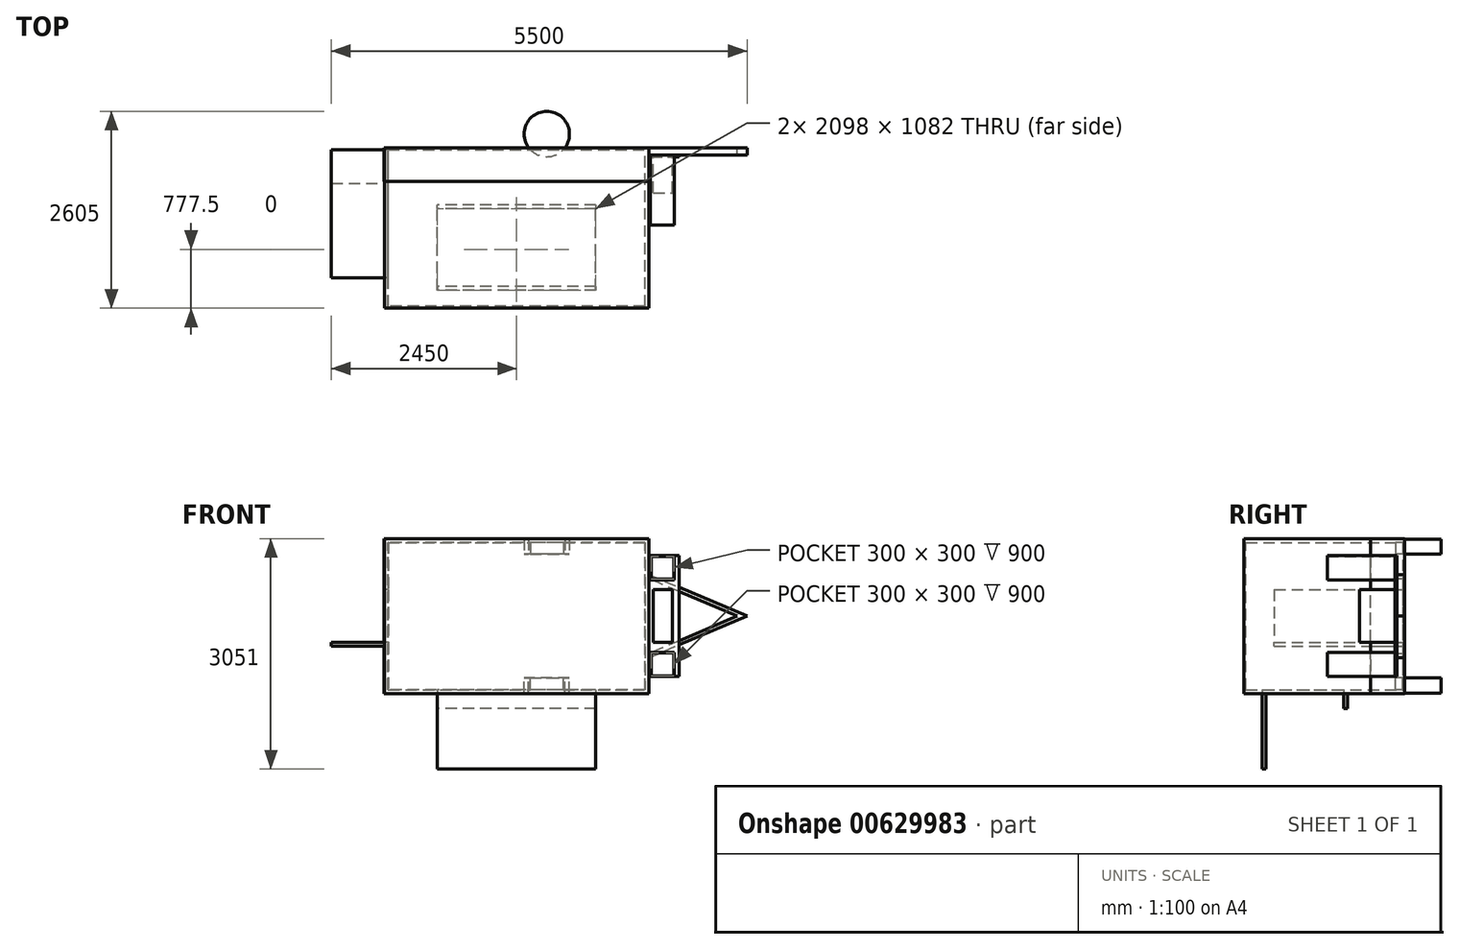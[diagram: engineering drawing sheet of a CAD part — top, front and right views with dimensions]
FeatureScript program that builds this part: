
annotation { "Feature Type Name" : "Feature", "Feature Type Description" : "" }
export const myFeature = defineFeature(function(context is Context, id is Id, definition is map)
    precondition{}
    {
        {
            var Q0;
            Q0=qCreatedBy(makeId("Front.planeOp"),FACE);
            var sketch = newSketch(context, id + "F0", { "sketchPlane" : qUnion([Q0])});
            skLineSegment(sketch, "E0.bottom", {"start": v(1750, -1025) * mm, "end": v(-1750, -1025) * mm});
            skLineSegment(sketch, "E0.top", {"start": v(1750, 1025) * mm, "end": v(-1750, 1025) * mm});
            skLineSegment(sketch, "E0.left", {"start": v(1750, -1025) * mm, "end": v(1750, 1025) * mm});
            skLineSegment(sketch, "E0.right", {"start": v(-1750, -1025) * mm, "end": v(-1750, 1025) * mm});
            skPoint(sketch, "E0.middle", {"position": v(0, 0) * mm});
            skLineSegment(sketch, "E1.0", {"start": v(1700, 975) * mm, "end": v(-1700, 975) * mm});
            skLineSegment(sketch, "E1.1", {"start": v(1700, -975) * mm, "end": v(1700, 975) * mm});
            skLineSegment(sketch, "E1.2", {"start": v(1700, -975) * mm, "end": v(-1700, -975) * mm});
            skLineSegment(sketch, "E1.3", {"start": v(-1700, -975) * mm, "end": v(-1700, 975) * mm});
            skSolve(sketch);
        }
        {
            var Q0;
            Q0=makeQuery(id+"F0.imprint","IMPRINT",FACE,{"disambiguationData":[TD([[makeQuery(id+"F0.imprint","IMPRINT",EDGE,{"derivedFrom":sQuery(id+"F0.wireOp",EDGE,"E0.bottom")}),-1.0]])]});
            var Q1;
            Q1=sQuery(id+"F0.wireOp",EDGE,"E0.top");
            var Q2;
            Q2=sQuery(id+"F0.wireOp",EDGE,"E0.right");
            var Q3;
            Q3=sQuery(id+"F0.wireOp",EDGE,"E0.bottom");
            var Q4;
            Q4=sQuery(id+"F0.wireOp",EDGE,"E0.left");
            extrude(context, id + "F1", {"entities" : qUnion([Q0]), "surfaceEntities" : qUnion([Q1, Q2, Q3, Q4]), "depth" : 2100 * mm, "offsetDistance" : 25 * mm});
        }
        {
            var Q0;
            Q0=makeQuery(id+"F1.opExtrude","SWEPT_FACE",FACE,{"disambiguationData":[OSD([sQuery(id+"F0.wireOp",EDGE,"E0.bottom")])]});
            var sketch = newSketch(context, id + "F2", { "sketchPlane" : qUnion([Q0])});
            skSolve(sketch);
        }
        {
            var Q0;
            Q0=qCreatedBy(makeId("Top.planeOp"),FACE);
            cPlane(context, id + "F3", {"entities" : qUnion([Q0]), "cplaneType" : CPlaneType.OFFSET, "offset" : 2040 * mm / 2 - 200 * mm, "width" : 150 * mm, "height" : 150 * mm});
        }
        {
            var Q0;
            Q0=qCreatedBy(id+"F3.planeOp",FACE);
            var sketch = newSketch(context, id + "F4", { "sketchPlane" : qUnion([Q0])});
            skCircle(sketch, "E2", {"center": v(400, 180) * mm, "radius": 300 * mm});
            skCircle(sketch, "E3.MirrorC", {"center": v(-400, 180) * mm, "radius": 300 * mm});
            skSolve(sketch);
        }
        {
            var Q0;
            Q0=makeQuery(id+"F4.imprint","IMPRINT",FACE,{"disambiguationData":[TD([[makeQuery(id+"F4.imprint","IMPRINT",EDGE,{"derivedFrom":sQuery(id+"F4.wireOp",EDGE,"E2")}),1.0]])]});
            var Q1;
            Q1=makeQuery(id+"F4.imprint","IMPRINT",FACE,{"disambiguationData":[TD([[makeQuery(id+"F4.imprint","IMPRINT",EDGE,{"derivedFrom":sQuery(id+"F4.wireOp",EDGE,"E3.MirrorC")}),-1.0]])]});
            extrude(context, id + "F5", {"entities" : qUnion([Q0, Q1]), "depth" : 200 * mm, "offsetDistance" : 25 * mm});
        }
        {
            var Q0;
            Q0=makeQuery(id+"F5.opExtrude","SWEPT_BODY",BODY,{"disambiguationData":[OSD([sQuery(id+"F4.wireOp",EDGE,"E3.MirrorC")])]});
            var Q1;
            Q1=makeQuery(id+"F5.opExtrude","SWEPT_BODY",BODY,{"disambiguationData":[OSD([sQuery(id+"F4.wireOp",EDGE,"E2")])]});
            var Q2;
            Q2=qCreatedBy(makeId("Top.planeOp"),FACE);
            mirror(context, id + "F6", {"entities" : qUnion([Q0, Q1]), "mirrorPlane" : qUnion([Q2])});
        }
        {
            var Q0;
            Q0=makeQuery(id+"F1.opExtrude","CAP_FACE",FACE,{"disambiguationData":[OSD([sQuery(id+"F0.wireOp",EDGE,"E0.bottom"),sQuery(id+"F0.wireOp",EDGE,"E0.top"),sQuery(id+"F0.wireOp",EDGE,"E0.left"),sQuery(id+"F0.wireOp",EDGE,"E0.right")])],"isStart":true});
            var sketch = newSketch(context, id + "F7", { "sketchPlane" : qUnion([Q0])});
            skLineSegment(sketch, "E4", {"start": v(0, 0) * mm, "end": v(-3050, 0) * mm, "construction": true});
            skLineSegment(sketch, "E5", {"start": v(-1750, 0) * mm, "end": v(-1750, 550) * mm, "construction": true});
            skLineSegment(sketch, "E6", {"start": v(-1750, 550) * mm, "end": v(-3050, 0) * mm});
            skLineSegment(sketch, "E7", {"start": v(-2921.68, 0) * mm, "end": v(-1750, 495.7) * mm});
            skLineSegment(sketch, "E8", {"start": v(-1750, 495.7) * mm, "end": v(-1750, 550) * mm});
            skLineSegment(sketch, "E9.MirrorCS", {"start": v(-2921.68, 0) * mm, "end": v(-1750, -495.7) * mm});
            skLineSegment(sketch, "E10.MirrorCS", {"start": v(-1750, -550) * mm, "end": v(-3050, 0) * mm});
            skLineSegment(sketch, "E11.MirrorCS", {"start": v(-1750, -495.7) * mm, "end": v(-1750, -550) * mm});
            skSolve(sketch);
        }
        {
            var Q0;
            Q0=makeQuery(id+"F7.imprint","IMPRINT",FACE,{"disambiguationData":[TD([[makeQuery(id+"F7.imprint","IMPRINT",EDGE,{"derivedFrom":sQuery(id+"F7.wireOp",EDGE,"E6")}),1.0]])]});
            extrude(context, id + "F8", {"entities" : qUnion([Q0]), "oppositeDirection" : true, "depth" : 100 * mm, "offsetDistance" : 25 * mm});
        }
        {
            var Q0;
            Q0=makeQuery(id+"F8.opExtrude","CAP_FACE",FACE,{"disambiguationData":[OSD([sQuery(id+"F7.wireOp",EDGE,"E6"),sQuery(id+"F7.wireOp",EDGE,"E7"),sQuery(id+"F7.wireOp",EDGE,"E8"),sQuery(id+"F7.wireOp",EDGE,"E9.MirrorCS"),sQuery(id+"F7.wireOp",EDGE,"E10.MirrorCS"),sQuery(id+"F7.wireOp",EDGE,"E11.MirrorCS")])],"isStart":false});
            var sketch = newSketch(context, id + "F9", { "sketchPlane" : qUnion([Q0])});
            skLineSegment(sketch, "E12.bottom", {"start": v(1810, -350) * mm, "end": v(2060, -350) * mm});
            skLineSegment(sketch, "E12.top", {"start": v(1810, 350) * mm, "end": v(2060, 350) * mm});
            skLineSegment(sketch, "E12.left", {"start": v(1810, -350) * mm, "end": v(1810, 350) * mm});
            skLineSegment(sketch, "E12.right", {"start": v(2060, -350) * mm, "end": v(2060, 350) * mm});
            skSolve(sketch);
        }
        {
            var Q0;
            {var subQ0=sQuery(id+"F9.wireOp",EDGE,"E12.right");var subQ1=sQuery(id+"F9.wireOp",EDGE,"E12.top");var subQ2=makeQuery(id+"F9.imprint","INTERSECT",VERTEX,{"derivedFrom":[subQ1,subQ0]});Q0=makeQuery(id+"F9.imprint","IMPRINT",FACE,{"disambiguationData":[TD([[makeQuery(id+"F9.imprint","IMPRINT",EDGE,{"disambiguationData":[TD([[subQ2,1.0]])],"derivedFrom":subQ1}),-1.0]])]});}
            var Q1;
            {var subQ0=sQuery(id+"F9.wireOp",EDGE,"E12.top");var subQ1=makeQuery(id+"F8.opExtrude","CAP_EDGE",EDGE,{"disambiguationData":[OSD([sQuery(id+"F7.wireOp",EDGE,"E7")])],"isStart":false});var subQ2=makeQuery(id+"F9.imprint","INTERSECT",VERTEX,{"derivedFrom":[subQ1,subQ0]});Q1=makeQuery(id+"F9.imprint","IMPRINT",FACE,{"disambiguationData":[TD([[makeQuery(id+"F9.imprint","IMPRINT",EDGE,{"disambiguationData":[TD([[subQ2,-1.0]])],"derivedFrom":subQ0}),-1.0]])]});}
            var Q2;
            {var subQ0=sQuery(id+"F9.wireOp",EDGE,"E12.top");var subQ7=sQuery(id+"F9.wireOp",EDGE,"E12.left");var subQ8=makeQuery(id+"F9.imprint","INTERSECT",VERTEX,{"derivedFrom":[subQ0,subQ7]});Q2=makeQuery(id+"F9.imprint","IMPRINT",FACE,{"disambiguationData":[TD([[makeQuery(id+"F9.imprint","IMPRINT",EDGE,{"disambiguationData":[TD([[subQ8,-1.0]])],"derivedFrom":subQ0}),-1.0]])]});}
            var Q3;
            {var subQ0=sQuery(id+"F9.wireOp",EDGE,"E12.left");var subQ1=makeQuery(id+"F8.opExtrude","CAP_EDGE",EDGE,{"disambiguationData":[OSD([sQuery(id+"F7.wireOp",EDGE,"E10.MirrorCS")])],"isStart":false});var subQ2=makeQuery(id+"F9.imprint","INTERSECT",VERTEX,{"derivedFrom":[subQ1,subQ0]});Q3=makeQuery(id+"F9.imprint","IMPRINT",FACE,{"disambiguationData":[TD([[makeQuery(id+"F9.imprint","IMPRINT",EDGE,{"disambiguationData":[TD([[subQ2,-1.0]])],"derivedFrom":subQ0}),-1.0]])]});}
            var Q4;
            {var subQ0=sQuery(id+"F9.wireOp",EDGE,"E12.bottom");Q4=makeQuery(id+"F9.imprint","IMPRINT",FACE,{"disambiguationData":[TD([[makeQuery(id+"F9.imprint","IMPRINT",EDGE,{"derivedFrom":subQ0}),1.0]])]});}
            extrude(context, id + "F10", {"entities" : qUnion([Q0, Q1, Q2, Q3, Q4]), "depth" : 500 * mm, "offsetDistance" : 25 * mm});
        }
        {
            var Q0;
            Q0=makeQuery(id+"F1.opExtrude","CAP_FACE",FACE,{"disambiguationData":[OSD([sQuery(id+"F0.wireOp",EDGE,"E0.bottom"),sQuery(id+"F0.wireOp",EDGE,"E0.top"),sQuery(id+"F0.wireOp",EDGE,"E0.left"),sQuery(id+"F0.wireOp",EDGE,"E0.right"),sQuery(id+"F0.wireOp",EDGE,"E1.0"),sQuery(id+"F0.wireOp",EDGE,"E1.1"),sQuery(id+"F0.wireOp",EDGE,"E1.2"),sQuery(id+"F0.wireOp",EDGE,"E1.3")])],"isStart":true});
            var sketch = newSketch(context, id + "F11", { "sketchPlane" : qUnion([Q0])});
            skLineSegment(sketch, "E13.bottom", {"start": v(1750, -1025) * mm, "end": v(-1750, -1025) * mm});
            skLineSegment(sketch, "E13.top", {"start": v(1750, 1025) * mm, "end": v(-1750, 1025) * mm});
            skLineSegment(sketch, "E13.left", {"start": v(1750, -1025) * mm, "end": v(1750, 1025) * mm});
            skLineSegment(sketch, "E13.right", {"start": v(-1750, -1025) * mm, "end": v(-1750, 1025) * mm});
            skSolve(sketch);
        }
        {
            var Q0;
            Q0 = qSketchRegion(id + "F11", true);
            extrude(context, id + "F12", {"entities" : qUnion([Q0]), "operationType" : NewBodyOperationType.ADD, "oppositeDirection" : true, "depth" : 25 * mm, "offsetDistance" : 25 * mm});
        }
        {
            var Q0;
            Q0=makeQuery(id+"F1.opExtrude","CAP_FACE",FACE,{"disambiguationData":[OSD([sQuery(id+"F0.wireOp",EDGE,"E0.bottom"),sQuery(id+"F0.wireOp",EDGE,"E0.top"),sQuery(id+"F0.wireOp",EDGE,"E0.left"),sQuery(id+"F0.wireOp",EDGE,"E0.right"),sQuery(id+"F0.wireOp",EDGE,"E1.0"),sQuery(id+"F0.wireOp",EDGE,"E1.1"),sQuery(id+"F0.wireOp",EDGE,"E1.2"),sQuery(id+"F0.wireOp",EDGE,"E1.3")])],"isStart":false});
            var sketch = newSketch(context, id + "F13", { "sketchPlane" : qUnion([Q0])});
            skLineSegment(sketch, "E14.bottom", {"start": v(-1750, 1025) * mm, "end": v(1750, 1025) * mm});
            skLineSegment(sketch, "E14.top", {"start": v(-1750, -1025) * mm, "end": v(1750, -1025) * mm});
            skLineSegment(sketch, "E14.left", {"start": v(-1750, 1025) * mm, "end": v(-1750, -1025) * mm});
            skLineSegment(sketch, "E14.right", {"start": v(1750, 1025) * mm, "end": v(1750, -1025) * mm});
            skSolve(sketch);
        }
        {
            var Q0;
            Q0 = qSketchRegion(id + "F13", true);
            extrude(context, id + "F14", {"entities" : qUnion([Q0]), "operationType" : NewBodyOperationType.ADD, "depth" : 25 * mm, "offsetDistance" : 25 * mm});
        }
        {
            var Q0;
            {var subQ0=sQuery(id+"F0.wireOp",EDGE,"E0.bottom");Q0=makeQuery(id+"F2.imprint","IMPRINT",FACE,{"disambiguationData":[TD([[makeQuery(id+"F2.imprint","IMPRINT",EDGE,{"derivedFrom":makeQuery(id+"F1.opExtrude","CAP_EDGE",EDGE,{"disambiguationData":[OSD([subQ0])],"isStart":true})}),-1.0]])]});}
            var sketch = newSketch(context, id + "F15", { "sketchPlane" : qUnion([Q0])});
            skLineSegment(sketch, "E15.bottom", {"start": v(1049, 1888.5) * mm, "end": v(-1049, 1888.5) * mm});
            skLineSegment(sketch, "E15.top", {"start": v(1049, 806.5) * mm, "end": v(-1049, 806.5) * mm});
            skLineSegment(sketch, "E15.left", {"start": v(1049, 1888.5) * mm, "end": v(1049, 806.5) * mm});
            skLineSegment(sketch, "E15.right", {"start": v(-1049, 1888.5) * mm, "end": v(-1049, 806.5) * mm});
            skSolve(sketch);
        }
        {
            var Q0;
            Q0=makeQuery(id+"F15.imprint","IMPRINT",FACE,{"disambiguationData":[TD([[makeQuery(id+"F15.imprint","IMPRINT",EDGE,{"derivedFrom":sQuery(id+"F15.wireOp",EDGE,"E15.bottom")}),1.0]])]});
            extrude(context, id + "F16", {"entities" : qUnion([Q0]), "operationType" : NewBodyOperationType.REMOVE, "oppositeDirection" : true, "depth" : 260 * mm, "offsetDistance" : 25 * mm});
        }
        {
            var Q0;
            Q0=makeQuery(id+"F14.boolean.opBoolean","MERGE",FACE,{"derivedFrom":[makeQuery(id+"F1.opExtrude","SWEPT_FACE",FACE,{"disambiguationData":[OSD([sQuery(id+"F0.wireOp",EDGE,"E0.right")])]}),makeQuery(id+"F14.opExtrude","SWEPT_FACE",FACE,{"disambiguationData":[OSD([sQuery(id+"F13.wireOp",EDGE,"E14.left")])]})]});
            var sketch = newSketch(context, id + "F17", { "sketchPlane" : qUnion([Q0])});
            skLineSegment(sketch, "E16.bottom", {"start": v(1725, 350) * mm, "end": v(25, 350) * mm});
            skLineSegment(sketch, "E16.top", {"start": v(1725, -350) * mm, "end": v(25, -350) * mm});
            skLineSegment(sketch, "E16.left", {"start": v(1725, 350) * mm, "end": v(1725, -350) * mm});
            skLineSegment(sketch, "E16.right", {"start": v(25, 350) * mm, "end": v(25, -350) * mm});
            skSolve(sketch);
        }
        {
            var Q0;
            Q0=makeQuery(id+"F17.imprint","IMPRINT",FACE,{"disambiguationData":[TD([[makeQuery(id+"F17.imprint","IMPRINT",EDGE,{"derivedFrom":sQuery(id+"F17.wireOp",EDGE,"E16.bottom")}),1.0]])]});
            extrude(context, id + "F18", {"entities" : qUnion([Q0]), "operationType" : NewBodyOperationType.REMOVE, "oppositeDirection" : true, "depth" : 150 * mm, "offsetDistance" : 25 * mm});
        }
        {
            var Q0;
            Q0=makeQuery(id+"F16.boolean.opBoolean","COPY",FACE,{"derivedFrom":makeQuery(id+"F16.opExtrude","SWEPT_FACE",FACE,{"disambiguationData":[OSD([sQuery(id+"F15.wireOp",EDGE,"E15.right")])]})});
            var sketch = newSketch(context, id + "F19", { "sketchPlane" : qUnion([Q0])});
            skLineSegment(sketch, "E17.bottom", {"start": v(-806.5, -1025) * mm, "end": v(-756.5, -1025) * mm});
            skLineSegment(sketch, "E17.top", {"start": v(-806.5, -1225) * mm, "end": v(-756.5, -1225) * mm});
            skLineSegment(sketch, "E17.left", {"start": v(-806.5, -1025) * mm, "end": v(-806.5, -1225) * mm});
            skLineSegment(sketch, "E17.right", {"start": v(-756.5, -1025) * mm, "end": v(-756.5, -1225) * mm});
            skSolve(sketch);
        }
        {
            var Q0;
            Q0=makeQuery(id+"F19.imprint","IMPRINT",FACE,{"disambiguationData":[TD([[makeQuery(id+"F19.imprint","IMPRINT",EDGE,{"derivedFrom":sQuery(id+"F19.wireOp",EDGE,"E17.bottom")}),-1.0]])]});
            var Q1;
            Q1=makeQuery(id+"F16.boolean.opBoolean","COPY",FACE,{"derivedFrom":makeQuery(id+"F16.opExtrude","SWEPT_FACE",FACE,{"disambiguationData":[OSD([sQuery(id+"F15.wireOp",EDGE,"E15.left")])]})});
            extrude(context, id + "F20", {"entities" : qUnion([Q0]), "endBound" : BoundingType.UP_TO_SURFACE, "depth" : 25 * mm, "endBoundEntityFace" : qUnion([Q1]), "offsetDistance" : 25 * mm});
        }
        {
            var Q0;
            Q0=makeQuery(id+"F16.boolean.opBoolean","COPY",FACE,{"derivedFrom":makeQuery(id+"F16.opExtrude","SWEPT_FACE",FACE,{"disambiguationData":[OSD([sQuery(id+"F15.wireOp",EDGE,"E15.right")])]})});
            var sketch = newSketch(context, id + "F21", { "sketchPlane" : qUnion([Q0])});
            skLineSegment(sketch, "E18.bottom", {"start": v(-1888.5, -1025) * mm, "end": v(-1888.5, -1025) * mm});
            skLineSegment(sketch, "E18.top", {"start": v(-1838.5, -2025) * mm, "end": v(-1888.5, -2025) * mm});
            skLineSegment(sketch, "E18.left", {"start": v(-1838.5, -1025) * mm, "end": v(-1838.5, -2025) * mm});
            skLineSegment(sketch, "E18.right", {"start": v(-1888.5, -1025) * mm, "end": v(-1888.5, -2025) * mm});
            skSolve(sketch);
        }
        {
            var Q0;
            Q0=makeQuery(id+"F21.imprint","IMPRINT",FACE,{"disambiguationData":[TD([[makeQuery(id+"F21.imprint","IMPRINT",EDGE,{"derivedFrom":sQuery(id+"F21.wireOp",EDGE,"E18.bottom")}),1.0]])]});
            var Q1;
            Q1=makeQuery(id+"F21.imprint","IMPRINT",FACE,{"disambiguationData":[TD([[makeQuery(id+"F21.imprint","IMPRINT",EDGE,{"derivedFrom":sQuery(id+"F21.wireOp",EDGE,"E18.top")}),-1.0]])]});
            var Q2;
            Q2=makeQuery(id+"F16.boolean.opBoolean","COPY",FACE,{"derivedFrom":makeQuery(id+"F16.opExtrude","SWEPT_FACE",FACE,{"disambiguationData":[OSD([sQuery(id+"F15.wireOp",EDGE,"E15.left")])]})});
            extrude(context, id + "F22", {"entities" : qUnion([Q0, Q1]), "endBound" : BoundingType.UP_TO_SURFACE, "depth" : 25 * mm, "endBoundEntityFace" : qUnion([Q2]), "offsetDistance" : 25 * mm});
        }
        {
            var Q0;
            Q0=makeQuery(id+"F18.boolean.opBoolean","MERGE",FACE,{"derivedFrom":[makeQuery(id+"F12.opExtrude","CAP_FACE",FACE,{"disambiguationData":[OSD([sQuery(id+"F11.wireOp",EDGE,"E13.bottom"),sQuery(id+"F11.wireOp",EDGE,"E13.top"),sQuery(id+"F11.wireOp",EDGE,"E13.left"),sQuery(id+"F11.wireOp",EDGE,"E13.right")])],"isStart":false}),makeQuery(id+"F18.opExtrude","SWEPT_FACE",FACE,{"disambiguationData":[OSD([sQuery(id+"F17.wireOp",EDGE,"E16.right")])]})]});
            var sketch = newSketch(context, id + "F23", { "sketchPlane" : qUnion([Q0])});
            skLineSegment(sketch, "E19.bottom", {"start": v(-1750, -350) * mm, "end": v(-2450, -350) * mm});
            skLineSegment(sketch, "E19.top", {"start": v(-1750, -400) * mm, "end": v(-2450, -400) * mm});
            skLineSegment(sketch, "E19.left", {"start": v(-1750, -350) * mm, "end": v(-1750, -400) * mm});
            skLineSegment(sketch, "E19.right", {"start": v(-2450, -350) * mm, "end": v(-2450, -400) * mm});
            skSolve(sketch);
        }
        {
            var Q0;
            Q0=makeQuery(id+"F23.imprint","IMPRINT",FACE,{"disambiguationData":[TD([[makeQuery(id+"F23.imprint","IMPRINT",EDGE,{"derivedFrom":sQuery(id+"F23.wireOp",EDGE,"E19.bottom")}),1.0]])]});
            var Q1;
            Q1=makeQuery(id+"F18.boolean.opBoolean","COPY",FACE,{"derivedFrom":makeQuery(id+"F18.opExtrude","SWEPT_FACE",FACE,{"disambiguationData":[OSD([sQuery(id+"F17.wireOp",EDGE,"E16.left")])]})});
            extrude(context, id + "F24", {"entities" : qUnion([Q0]), "endBound" : BoundingType.UP_TO_SURFACE, "depth" : 25 * mm, "endBoundEntityFace" : qUnion([Q1]), "offsetDistance" : 25 * mm});
        }
        {
            var Q0;
            Q0=makeQuery(id+"F8.opExtrude","CAP_FACE",FACE,{"disambiguationData":[OSD([sQuery(id+"F7.wireOp",EDGE,"E6"),sQuery(id+"F7.wireOp",EDGE,"E7"),sQuery(id+"F7.wireOp",EDGE,"E8"),sQuery(id+"F7.wireOp",EDGE,"E9.MirrorCS"),sQuery(id+"F7.wireOp",EDGE,"E10.MirrorCS"),sQuery(id+"F7.wireOp",EDGE,"E11.MirrorCS")])],"isStart":false});
            var sketch = newSketch(context, id + "F25", { "sketchPlane" : qUnion([Q0])});
            skLineSegment(sketch, "E20.bottom", {"start": v(1750, 800) * mm, "end": v(2150, 800) * mm});
            skLineSegment(sketch, "E20.top", {"start": v(1750, -800) * mm, "end": v(2150, -800) * mm});
            skLineSegment(sketch, "E20.left", {"start": v(1750, 800) * mm, "end": v(1750, -800) * mm});
            skLineSegment(sketch, "E20.right", {"start": v(2150, 800) * mm, "end": v(2150, -800) * mm});
            skSolve(sketch);
        }
        {
            var Q0;
            {var subQ0=sQuery(id+"F25.wireOp",EDGE,"E20.top");Q0=makeQuery(id+"F25.imprint","IMPRINT",FACE,{"disambiguationData":[TD([[makeQuery(id+"F25.imprint","IMPRINT",EDGE,{"derivedFrom":subQ0}),1.0]])]});}
            var Q1;
            {var subQ0=sQuery(id+"F25.wireOp",EDGE,"E20.left");var subQ1=makeQuery(id+"F8.opExtrude","CAP_EDGE",EDGE,{"disambiguationData":[OSD([sQuery(id+"F7.wireOp",EDGE,"E7")])],"isStart":false});var subQ2=makeQuery(id+"F25.imprint","INTERSECT",VERTEX,{"derivedFrom":[subQ1,subQ0]});Q1=makeQuery(id+"F25.imprint","IMPRINT",FACE,{"disambiguationData":[TD([[makeQuery(id+"F25.imprint","IMPRINT",EDGE,{"disambiguationData":[TD([[subQ2,-1.0]])],"derivedFrom":subQ0}),1.0]])]});}
            var Q2;
            {var subQ0=sQuery(id+"F25.wireOp",EDGE,"E20.left");var subQ1=makeQuery(id+"F8.opExtrude","CAP_EDGE",EDGE,{"disambiguationData":[OSD([sQuery(id+"F7.wireOp",EDGE,"E6")])],"isStart":false});var subQ2=makeQuery(id+"F25.imprint","INTERSECT",VERTEX,{"derivedFrom":[subQ1,subQ0]});Q2=makeQuery(id+"F25.imprint","IMPRINT",FACE,{"disambiguationData":[TD([[makeQuery(id+"F25.imprint","IMPRINT",EDGE,{"disambiguationData":[TD([[subQ2,-1.0]])],"derivedFrom":subQ0}),1.0]])]});}
            var Q3;
            {var subQ0=sQuery(id+"F25.wireOp",EDGE,"E20.bottom");Q3=makeQuery(id+"F25.imprint","IMPRINT",FACE,{"disambiguationData":[TD([[makeQuery(id+"F25.imprint","IMPRINT",EDGE,{"derivedFrom":subQ0}),-1.0]])]});}
            var Q4;
            {var subQ0=sQuery(id+"F25.wireOp",EDGE,"E20.left");var subQ1=makeQuery(id+"F8.opExtrude","CAP_EDGE",EDGE,{"disambiguationData":[OSD([sQuery(id+"F7.wireOp",EDGE,"E9.MirrorCS")])],"isStart":false});var subQ2=makeQuery(id+"F25.imprint","INTERSECT",VERTEX,{"derivedFrom":[subQ1,subQ0]});Q4=makeQuery(id+"F25.imprint","IMPRINT",FACE,{"disambiguationData":[TD([[makeQuery(id+"F25.imprint","IMPRINT",EDGE,{"disambiguationData":[TD([[subQ2,-1.0]])],"derivedFrom":subQ0}),1.0]])]});}
            var Q5;
            {var subQ0=sQuery(id+"F25.wireOp",EDGE,"E20.left");var subQ1=makeQuery(id+"F8.opExtrude","CAP_EDGE",EDGE,{"disambiguationData":[OSD([sQuery(id+"F7.wireOp",EDGE,"E6")])],"isStart":false});var subQ2=makeQuery(id+"F25.imprint","INTERSECT",VERTEX,{"derivedFrom":[subQ1,subQ0]});var subQ3=makeQuery(id+"F8.opExtrude","CAP_EDGE",EDGE,{"disambiguationData":[OSD([sQuery(id+"F7.wireOp",EDGE,"E7")])],"isStart":false});var subQ4=makeQuery(id+"F25.imprint","INTERSECT",VERTEX,{"derivedFrom":[subQ3,subQ0]});Q5=makeQuery(id+"F25.imprint","IMPRINT",FACE,{"disambiguationData":[TD([[makeQuery(id+"F25.imprint","IMPRINT",EDGE,{"disambiguationData":[TD([[subQ2,1.0],[subQ4,-1.0]])],"derivedFrom":subQ0}),-1.0]])]});}
            var Q6;
            {var subQ0=sQuery(id+"F25.wireOp",EDGE,"E20.left");var subQ1=makeQuery(id+"F8.opExtrude","CAP_EDGE",EDGE,{"disambiguationData":[OSD([sQuery(id+"F7.wireOp",EDGE,"E9.MirrorCS")])],"isStart":false});var subQ2=makeQuery(id+"F25.imprint","INTERSECT",VERTEX,{"derivedFrom":[subQ1,subQ0]});var subQ3=makeQuery(id+"F8.opExtrude","CAP_EDGE",EDGE,{"disambiguationData":[OSD([sQuery(id+"F7.wireOp",EDGE,"E10.MirrorCS")])],"isStart":false});var subQ4=makeQuery(id+"F25.imprint","INTERSECT",VERTEX,{"derivedFrom":[subQ3,subQ0]});Q6=makeQuery(id+"F25.imprint","IMPRINT",FACE,{"disambiguationData":[TD([[makeQuery(id+"F25.imprint","IMPRINT",EDGE,{"disambiguationData":[TD([[subQ2,1.0],[subQ4,-1.0]])],"derivedFrom":subQ0}),-1.0]])]});}
            extrude(context, id + "F26", {"entities" : qUnion([Q0, Q1, Q2, Q3, Q4, Q5, Q6]), "depth" : 25 * mm, "offsetDistance" : 25 * mm});
        }
        {
            var Q0;
            Q0=makeQuery(id+"F26.opExtrude","CAP_FACE",FACE,{"disambiguationData":[OSD([sQuery(id+"F25.wireOp",EDGE,"E20.bottom"),sQuery(id+"F25.wireOp",EDGE,"E20.top"),sQuery(id+"F25.wireOp",EDGE,"E20.left"),sQuery(id+"F25.wireOp",EDGE,"E20.right")])],"isStart":false});
            var sketch = newSketch(context, id + "F27", { "sketchPlane" : qUnion([Q0])});
            skLineSegment(sketch, "E21.bottom", {"start": v(1770, 800) * mm, "end": v(2090, 800) * mm});
            skLineSegment(sketch, "E21.top", {"start": v(1770, 480) * mm, "end": v(2090, 480) * mm});
            skLineSegment(sketch, "E21.left", {"start": v(1770, 800) * mm, "end": v(1770, 480) * mm});
            skLineSegment(sketch, "E21.right", {"start": v(2090, 800) * mm, "end": v(2090, 480) * mm});
            skLineSegment(sketch, "E22.0", {"start": v(1780, 790) * mm, "end": v(2080, 790) * mm});
            skLineSegment(sketch, "E22.1", {"start": v(1780, 790) * mm, "end": v(1780, 490) * mm});
            skLineSegment(sketch, "E22.2", {"start": v(1780, 490) * mm, "end": v(2080, 490) * mm});
            skLineSegment(sketch, "E22.3", {"start": v(2080, 790) * mm, "end": v(2080, 490) * mm});
            skLineSegment(sketch, "E23.MirrorCS", {"start": v(1770, -800) * mm, "end": v(2090, -800) * mm});
            skLineSegment(sketch, "E24.MirrorCS", {"start": v(1780, -790) * mm, "end": v(2080, -790) * mm});
            skLineSegment(sketch, "E25.MirrorCS", {"start": v(1770, -800) * mm, "end": v(1770, -480) * mm});
            skLineSegment(sketch, "E26.MirrorCS", {"start": v(1780, -790) * mm, "end": v(1780, -490) * mm});
            skLineSegment(sketch, "E27.MirrorCS", {"start": v(1780, -490) * mm, "end": v(2080, -490) * mm});
            skLineSegment(sketch, "E28.MirrorCS", {"start": v(1770, -480) * mm, "end": v(2090, -480) * mm});
            skLineSegment(sketch, "E29.MirrorCS", {"start": v(2080, -790) * mm, "end": v(2080, -490) * mm});
            skLineSegment(sketch, "E30.MirrorCS", {"start": v(2090, -800) * mm, "end": v(2090, -480) * mm});
            skSolve(sketch);
        }
        {
            var Q0;
            Q0=makeQuery(id+"F27.imprint","IMPRINT",FACE,{"disambiguationData":[TD([[makeQuery(id+"F27.imprint","IMPRINT",EDGE,{"derivedFrom":sQuery(id+"F27.wireOp",EDGE,"E21.bottom")}),-1.0]])]});
            var Q1;
            Q1=makeQuery(id+"F27.imprint","IMPRINT",FACE,{"disambiguationData":[TD([[makeQuery(id+"F27.imprint","IMPRINT",EDGE,{"derivedFrom":sQuery(id+"F27.wireOp",EDGE,"E23.MirrorCS")}),1.0]])]});
            extrude(context, id + "F28", {"entities" : qUnion([Q0, Q1]), "operationType" : NewBodyOperationType.ADD, "depth" : 900 * mm, "offsetDistance" : 25 * mm});
        }
        {
            var Q0;
            Q0=makeQuery(id+"F24.opExtrude","SWEPT_FACE",FACE,{"disambiguationData":[OSD([sQuery(id+"F23.wireOp",EDGE,"E19.top")])]});
            var sketch = newSketch(context, id + "F29", { "sketchPlane" : qUnion([Q0])});
            skLineSegment(sketch, "E31.bottom", {"start": v(-2450, 25) * mm, "end": v(-1750, 25) * mm});
            skLineSegment(sketch, "E31.top", {"start": v(-2450, 475) * mm, "end": v(-1750, 475) * mm});
            skLineSegment(sketch, "E31.left", {"start": v(-2450, 25) * mm, "end": v(-2450, 475) * mm});
            skLineSegment(sketch, "E31.right", {"start": v(-1750, 25) * mm, "end": v(-1750, 475) * mm});
            skSolve(sketch);
        }
        {
            var Q0;
            Q0=makeQuery(id+"F29.imprint","IMPRINT",FACE,{"disambiguationData":[TD([[makeQuery(id+"F29.imprint","IMPRINT",EDGE,{"derivedFrom":sQuery(id+"F29.wireOp",EDGE,"E31.bottom")}),-1.0]])]});
            extrude(context, id + "F30", {"entities" : qUnion([Q0]), "depth" : 1 * mm, "offsetDistance" : 25 * mm});
        }
        {
            var Q0;
            Q0=makeQuery(id+"F14.boolean.opBoolean","MERGE",FACE,{"derivedFrom":[makeQuery(id+"F1.opExtrude","SWEPT_FACE",FACE,{"disambiguationData":[OSD([sQuery(id+"F0.wireOp",EDGE,"E0.right")])]}),makeQuery(id+"F14.opExtrude","SWEPT_FACE",FACE,{"disambiguationData":[OSD([sQuery(id+"F13.wireOp",EDGE,"E14.left")])]})]});
            var sketch = newSketch(context, id + "F31", { "sketchPlane" : qUnion([Q0])});
            skLineSegment(sketch, "E32.bottom", {"start": v(0, 1025) * mm, "end": v(450, 1025) * mm});
            skLineSegment(sketch, "E32.top", {"start": v(0, -1025) * mm, "end": v(450, -1025) * mm});
            skLineSegment(sketch, "E32.left", {"start": v(0, 1025) * mm, "end": v(0, -1025) * mm});
            skLineSegment(sketch, "E32.right", {"start": v(450, 1025) * mm, "end": v(450, -1025) * mm});
            skSolve(sketch);
        }
        {
            var Q0;
            {var subQ1=sQuery(id+"F31.wireOp",EDGE,"E32.bottom");Q0=makeQuery(id+"F31.imprint","IMPRINT",FACE,{"disambiguationData":[TD([[makeQuery(id+"F31.imprint","IMPRINT",EDGE,{"derivedFrom":subQ1}),1.0]])]});}
            extrude(context, id + "F32", {"entities" : qUnion([Q0]), "depth" : 1 * mm, "offsetDistance" : 25 * mm});
        }
        {
            var Q0;
            Q0=makeQuery(id+"F14.boolean.opBoolean","MERGE",FACE,{"derivedFrom":[makeQuery(id+"F1.opExtrude","SWEPT_FACE",FACE,{"disambiguationData":[OSD([sQuery(id+"F0.wireOp",EDGE,"E0.top")])]}),makeQuery(id+"F14.opExtrude","SWEPT_FACE",FACE,{"disambiguationData":[OSD([sQuery(id+"F13.wireOp",EDGE,"E14.bottom")])]})]});
            var sketch = newSketch(context, id + "F33", { "sketchPlane" : qUnion([Q0])});
            skLineSegment(sketch, "E33.bottom", {"start": v(1750, 0) * mm, "end": v(-1750, 0) * mm});
            skLineSegment(sketch, "E33.top", {"start": v(1750, -450) * mm, "end": v(-1750, -450) * mm});
            skLineSegment(sketch, "E33.left", {"start": v(1750, 0) * mm, "end": v(1750, -450) * mm});
            skLineSegment(sketch, "E33.right", {"start": v(-1750, 0) * mm, "end": v(-1750, -450) * mm});
            skSolve(sketch);
        }
        {
            var Q0;
            Q0=makeQuery(id+"F33.imprint","IMPRINT",FACE,{"disambiguationData":[TD([[makeQuery(id+"F33.imprint","IMPRINT",EDGE,{"derivedFrom":sQuery(id+"F33.wireOp",EDGE,"E33.bottom")}),1.0]])]});
            extrude(context, id + "F34", {"entities" : qUnion([Q0]), "depth" : 1 * mm, "offsetDistance" : 25 * mm});
        }
        {
            var Q0;
            Q0=makeQuery(id+"F14.boolean.opBoolean","MERGE",FACE,{"derivedFrom":[makeQuery(id+"F1.opExtrude","SWEPT_FACE",FACE,{"disambiguationData":[OSD([sQuery(id+"F0.wireOp",EDGE,"E0.bottom")])]}),makeQuery(id+"F14.opExtrude","SWEPT_FACE",FACE,{"disambiguationData":[OSD([sQuery(id+"F13.wireOp",EDGE,"E14.top")])]})]});
            var sketch = newSketch(context, id + "F35", { "sketchPlane" : qUnion([Q0])});
            skLineSegment(sketch, "E34.bottom", {"start": v(1750, 0) * mm, "end": v(-1750, 0) * mm});
            skLineSegment(sketch, "E34.top", {"start": v(1750, 450) * mm, "end": v(-1750, 450) * mm});
            skLineSegment(sketch, "E34.left", {"start": v(1750, 0) * mm, "end": v(1750, 450) * mm});
            skLineSegment(sketch, "E34.right", {"start": v(-1750, 0) * mm, "end": v(-1750, 450) * mm});
            skSolve(sketch);
        }
        {
            var Q0;
            Q0=makeQuery(id+"F35.imprint","IMPRINT",FACE,{"disambiguationData":[TD([[makeQuery(id+"F35.imprint","IMPRINT",EDGE,{"derivedFrom":sQuery(id+"F35.wireOp",EDGE,"E34.bottom")}),-1.0]])]});
            extrude(context, id + "F36", {"entities" : qUnion([Q0]), "depth" : 1 * mm, "offsetDistance" : 25 * mm});
        }
        {
            var Q0;
            Q0=makeQuery(id+"F14.boolean.opBoolean","MERGE",FACE,{"derivedFrom":[makeQuery(id+"F1.opExtrude","SWEPT_FACE",FACE,{"disambiguationData":[OSD([sQuery(id+"F0.wireOp",EDGE,"E0.left")])]}),makeQuery(id+"F14.opExtrude","SWEPT_FACE",FACE,{"disambiguationData":[OSD([sQuery(id+"F13.wireOp",EDGE,"E14.right")])]})]});
            var sketch = newSketch(context, id + "F37", { "sketchPlane" : qUnion([Q0])});
            skLineSegment(sketch, "E35.bottom", {"start": v(0, -1025) * mm, "end": v(-450, -1025) * mm});
            skLineSegment(sketch, "E35.top", {"start": v(0, 1025) * mm, "end": v(-450, 1025) * mm});
            skLineSegment(sketch, "E35.left", {"start": v(0, -1025) * mm, "end": v(0, 1025) * mm});
            skLineSegment(sketch, "E35.right", {"start": v(-450, -1025) * mm, "end": v(-450, 1025) * mm});
            skSolve(sketch);
        }
        {
            var Q0;
            Q0=makeQuery(id+"F37.imprint","IMPRINT",FACE,{"disambiguationData":[TD([[makeQuery(id+"F37.imprint","IMPRINT",EDGE,{"derivedFrom":sQuery(id+"F37.wireOp",EDGE,"E35.bottom")}),1.0]])]});
            extrude(context, id + "F38", {"entities" : qUnion([Q0]), "depth" : 1 * mm, "offsetDistance" : 25 * mm});
        }
        {
            var Q0;
            Q0=makeQuery(id+"F18.boolean.opBoolean","MERGE",FACE,{"derivedFrom":[makeQuery(id+"F12.opExtrude","CAP_FACE",FACE,{"disambiguationData":[OSD([sQuery(id+"F11.wireOp",EDGE,"E13.bottom"),sQuery(id+"F11.wireOp",EDGE,"E13.top"),sQuery(id+"F11.wireOp",EDGE,"E13.left"),sQuery(id+"F11.wireOp",EDGE,"E13.right")])],"isStart":false})],"fromTools":[makeQuery(id+"F18.opExtrude","SWEPT_FACE",FACE,{"disambiguationData":[OSD([sQuery(id+"F17.wireOp",EDGE,"E16.right")])]})]});
            extrude(context, id + "F39", {"entities" : qUnion([Q0]), "depth" : 0.5 * mm, "offsetDistance" : 25 * mm});
        }
        {
            var Q0;
            Q0=makeQuery(id+"F1.opExtrude","SWEPT_FACE",FACE,{"disambiguationData":[OSD([sQuery(id+"F0.wireOp",EDGE,"E1.2")])]});
            extrude(context, id + "F40", {"entities" : qUnion([Q0]), "depth" : 0.5 * mm, "offsetDistance" : 25 * mm});
        }
        {
            var Q0;
            Q0=makeQuery(id+"F1.opExtrude","SWEPT_FACE",FACE,{"disambiguationData":[OSD([sQuery(id+"F0.wireOp",EDGE,"E1.1")])]});
            extrude(context, id + "F41", {"entities" : qUnion([Q0]), "depth" : 0.5 * mm, "offsetDistance" : 25 * mm});
        }
        {
            var Q0;
            Q0=makeQuery(id+"F1.opExtrude","SWEPT_FACE",FACE,{"disambiguationData":[OSD([sQuery(id+"F0.wireOp",EDGE,"E1.0")])]});
            extrude(context, id + "F42", {"entities" : qUnion([Q0]), "depth" : 0.5 * mm, "offsetDistance" : 25 * mm});
        }
        {
            var Q0;
            Q0=makeQuery(id+"F14.opExtrude","CAP_FACE",FACE,{"disambiguationData":[OSD([sQuery(id+"F13.wireOp",EDGE,"E14.bottom"),sQuery(id+"F13.wireOp",EDGE,"E14.top"),sQuery(id+"F13.wireOp",EDGE,"E14.left"),sQuery(id+"F13.wireOp",EDGE,"E14.right")])],"isStart":true});
            extrude(context, id + "F43", {"entities" : qUnion([Q0]), "depth" : 0.5 * mm, "offsetDistance" : 25 * mm});
        }
        {
            var Q0;
            Q0=makeQuery(id+"F1.opExtrude","SWEPT_FACE",FACE,{"disambiguationData":[OSD([sQuery(id+"F0.wireOp",EDGE,"E1.3")])]});
            extrude(context, id + "F44", {"entities" : qUnion([Q0]), "depth" : 0.5 * mm, "offsetDistance" : 25 * mm});
        }
    });
